# Revit family: ledhighbay-p5_240w-dali_ble2-840-w_545001062700_4d5e
name_source: partatom
category: Leuchten
revit_build: Autodesk Revit 2016 (Build: 20190508_0715(x64)
units: mm (PartAtom-declared; Revit-internal decimal feet)

## family parameters
Basisbauteil = Fläche
Beim Laden mit Abzugskörper schneiden = Nein
Bemaßung runder Anschluss = Durchmesser verwenden
Gemeinsam genutzt = Nein
Lichtquelle = Nein
Raumberechnungspunkt = Nein
Teiletyp = Normal

## types (1)
- LEDHighbay-P5 240W-DALI+BLE2-840-W (1 x LED, 38400 lm, 4000)
    Approval mark = CE, ENEC
    Beschreibung = High quality LED Highbay solution with improved ultra slim design. Improved efficacy of 160 lm/W. Equipped with breather to prevent condensation. Equipped with IP68 connector.
    CIE Flux Codes = 58 91 99 100 100
    Color Rendering = 80
    Color Temperature = 4000
    Control Gear = Electronic ballast
    Frequency = 60 Hz
    Height = 149 mm
    Hersteller = OPPLE
    Lamp Light Flux = 38400 lm
    Lamp count = 1
    Lampe = 1 x LED
    Length = 408 mm
    Luminous efficacy = 160 lm/W
    ModVariant = Nein
    Modell = 545001062700
    Mounting Place = Ceiling, Pole
    Mounting Type = Pendant
    Number of Poles = 1
    OnlyDefault = Ja
    Power Factor = 1
    Product Name = LEDHighbay-P5 240W-DALI+BLE2-840-W
    Product group = Pendant luminaire
    ProductGroupID = 9
    Protection Class = Protection class I
    Protection Degree = IP 66
    RLX_Detail_Level = 1
    RlxData = <blob elided: 242861 chars, md5=971886ad>
    Scheinlast = 240 VA
    Socket = socket
    Standby Power = 0 W
    System Light Flux = 38323 lm
    System Power = 240 W
    Typenbild = web_hb_p5_v2.jpg
    Typenkommentare = Product without accessories
    URL = http://relux.com
    VarID = ---
    Voltage = 230 V
    Voltage Range = 220-240 V
    Vorgabe-Ansicht = 1800 mm
    Weight = 0.00 kg
    Width = 408 mm

## geometry (parser evidence)
native form markers: Sweep x12
no freeform markers — native parametric forms only
